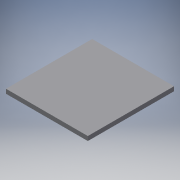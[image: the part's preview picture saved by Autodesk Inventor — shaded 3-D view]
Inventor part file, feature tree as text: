
AUTODESK INVENTOR PART (.ipt)
format: ipt  version: 2018.3 (Build 223284000, 284)  size: 82,944 bytes
history: native  units: mm
features: extrude x1, sketch x1
ambient origin geometry x8: Origin, YZ Plane, XZ Plane, XY Plane, X Axis, Y Axis, Z Axis, Center Point
bodies: Solid1 (feature_tree)
feature tree (2):
  extrude  "Extrusion1"  Depth=40.0mm
  sketch  "Sketch1"  dims[d0=38.0mm d1=40.0mm d2=2.0mm d3=0.0mm]
